# Revit family: KR6105551 Dispensador de jabon Koral mate black
name_source: partatom
category: Furniture
units: mm (PartAtom-declared; Revit-internal decimal feet)

## family parameters
Always vertical = Yes
Cut with Voids When Loaded = No
Host = Wall
Room Calculation Point = No
Shared = No

## types (1)
- Mate black
    Colección = Accesorios
    Creado por = IDD
    Description = Instala en tu baño el dispensador de jabón Koral, que se convertirá en el complemento ideal para tu grifería y es combinable con las demás piezas de accesorios Koral. Con resistencia a la carga hasta de 9kg. ¡Adquiérelo ahora!
    Fecha de creación = 09/10/2020
    Garantía = 30 años en estructura
    Garantía Acabados = 3 años en acabado
    Línea = Mate black
    Manufacturer = Corona
    Material = Corona_Acero_Negro Mate
    Peso Neto aprox = 500 g
    Referencia = KR6105551
    Resistencia = Resistente a la corrosión, pelado y decoloración por agua.
    Resistencia a cargas = 9 Kg - 19,8 lb
    Temperaturas máxima de trabajo = 40˚C / 104˚F
    Temperaturas mínima de trabajo = 4˚C / 39,2˚F
    URL = https://corona.co

## geometry (parser evidence)
native form markers: Sweep x7
no freeform markers — native parametric forms only
